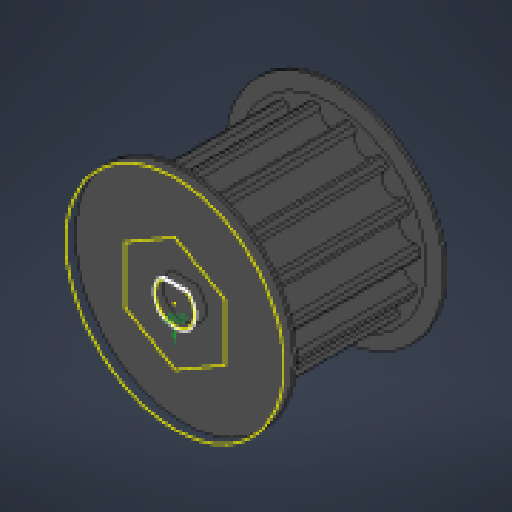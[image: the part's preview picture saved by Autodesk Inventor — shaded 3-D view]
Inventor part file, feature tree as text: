
AUTODESK INVENTOR PART (.ipt)
format: ipt  version: 2024 (Build 280153000, 153)  size: 470,528 bytes
history: native  units: in
note: dims shown in document units (in); Inventor stores cm internally (conversion verified against a paired STEP export)
features: other x6, extrude x3, boolean_combine x1, sketch x1, reference x1
ambient origin geometry x8: Origin, YZ Plane, XZ Plane, XY Plane, X Axis, Y Axis, Z Axis, Center Point
bodies: Solid1 (feature_tree), Solid2 (feature_tree), Solid3 (feature_tree)
feature tree (12):
  boolean_combine  "Combine1"
  sketch  "Sketch1"  dims[d0=0.0098in d1=0.05in d2=0.0in d3=0.05in d4=0.0in d5=0.05in d6=0.0in]
  extrude  "Extrusion1"  Depth=0.05in TaperAngle=0.0deg
  extrude  "Extrusion2"  Depth=0.05in TaperAngle=0.0deg
  extrude  "Extrusion3"  Depth=0.05in TaperAngle=0.0deg
  reference  "Reference1"
  other  "Cut-Revolve1[2]"
  other  "Cut-Extrude4"
  other  "Cut-Extrude5"
  other  "<userpath>\CodingProjects\C-AAM\CAD\V1\Base.iam"
  other  "Base.iam"
  other  "6627T91_Stepper Motor:1"
